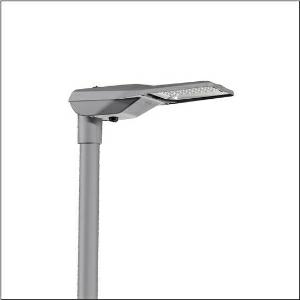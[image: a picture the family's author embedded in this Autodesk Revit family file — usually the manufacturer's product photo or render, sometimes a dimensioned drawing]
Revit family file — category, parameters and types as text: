
# Revit family: streetlight_sl_21_mini___stw1_0a_5xe2e33t08gb_f20d
name_source: partatom
category: Lighting Fixtures
units: mm (PartAtom-declared; Revit-internal decimal feet)

## family parameters
Cut with Voids When Loaded = No
Host = Face
Light Source = No
Part Type = Normal
Room Calculation Point = No
Round Connector Dimension = Use Diameter
Shared = No

## types (1)
- --- (1 x LED, 5940 lm, 40.4 W, 3000K)
    Apparent Load = 40 VA
    CIE Flux Codes = 38 75 98 100 100
    Color Rendering = 70
    Color Temperature = 3000K
    Default Elevation = 1800 mm
    Description = Streetlight SL 21 mini, mast luminaire, primary light control with lens, of PMMA, primary optical cover: cover, of toughened safety glass, transparent, light distribution: STW1.0a, light emission: direct distribution, primary light characteristic: asymmetric, installation type: side-entry, post-top, LED, High Power LED, rated luminous flux: 5.940lm, luminous efficacy: 147lm/W, light colour: 730, colour temperature: 3000K, control gear: D4i, control: overheat protection, constant luminous flux control, time-dependent luminous flux control, flexible luminous flux parameterisation, pre-setting: logarithmic dimming characteristic, mains connection: 220..240V, AC, 50/60Hz, start of lifetime: 40W, end of service life: 41W, reduction: 19W, luminaire housing, of diecast aluminium, powder-coated, SITECO metallic grey (DB 702S), corrosivity category C5 high according to DIN EN ISO 12944, please order mast flange separately, inclination adjustable: 0°, 5°, 10°, 15°, sealing non-destructively replaceable, multi-level sealing system, length: 628mm, width: 235mm, height: 110mm, mast flange for spigot size: 42mm (side-entry): 5XC10008XM4, 60/48mm (side-entry/post-top): 5XC10108XM2, 76/60mm (side-entry/post-top): 5XC10108XM1, mounting height: 4..8m, Smart Interface below and above, protection rating (complete): IP66, insulation class (complete): insulation class II (safety insulation), certification: CE, ENEC, ENEC+, VDE, impact resistance: IK10, permissible operating ambient temperature for outdoor applications: -40..+50°C, standard-compliant lighting for roads and squares, packaging unit: 1 piece

Light Distribution: STW1.0a
    Height = 110 mm
    Lamp = 1 x LED
    Lamp Light Flux = 5940 lm
    Lamp Power = 40.4 W
    Lamp count = 1
    Length = 625 mm
    Luminous efficacy = 147 lm/W
    Manufacturer = Siteco
    ModVariant = No
    Model = 5XE2E33T08GB
    Number of Poles = 1
    OnlyDefault = Yes
    Power Factor = 1
    Product Name = Streetlight SL 21 mini | STW1.0a
    Product group = mast luminaire | pylon top
    ProductGroupID = 6100
    Protection Class = Protection class II
    Protection Degree = IP 66
    RLX_Detail_Level = 1
    RLX_Emergency_Light_Flux = 0 lm
    RLX_Emergency_Type = 0
    RLX_Emergency_Type_DB = No
    RlxData = <blob elided: 26425 chars, md5=6b058be1>
    Socket = socket
    Standby Power = 0 W
    System Light Flux = 5940 lm
    System Power = 40 W
    Type Comments = factory setting: luminous flux: 100 % | dim-lin: 254 | 812 mA
    Type Image = l_1003514.jpg
    URL = http://relux.com
    VarID = @adj_184761
    Voltage = 0 V
    Weight = 0.00 kg
    Width = 234 mm

## geometry (parser evidence)
native form markers: Blend x4, Sweep x9
no freeform markers — native parametric forms only
